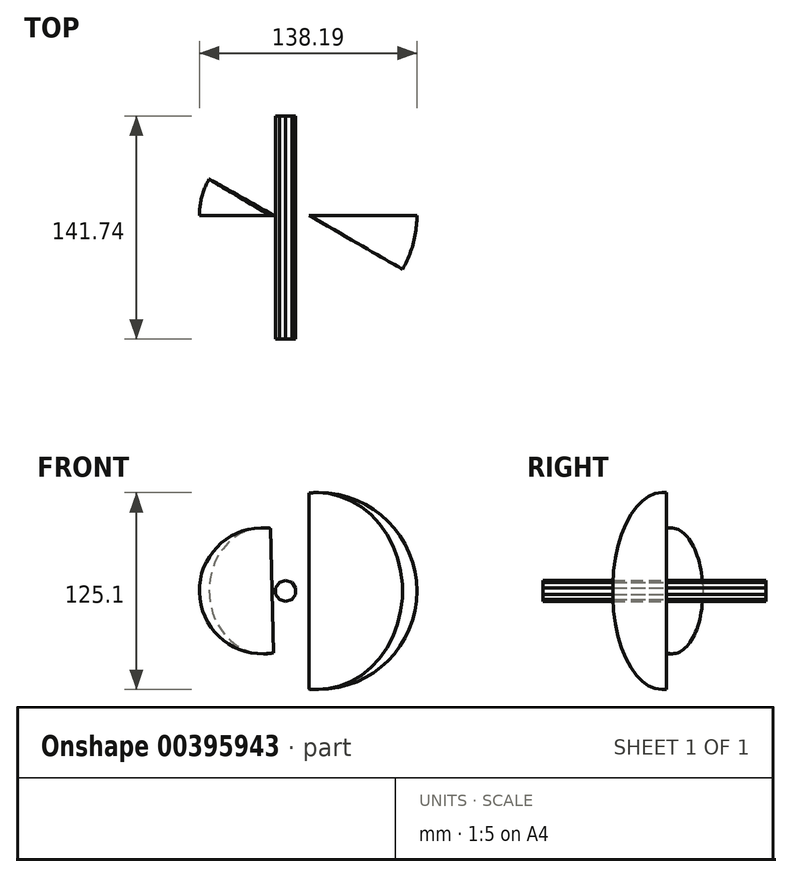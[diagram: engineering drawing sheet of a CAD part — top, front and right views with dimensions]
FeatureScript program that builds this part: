
annotation { "Feature Type Name" : "Feature", "Feature Type Description" : "" }
export const myFeature = defineFeature(function(context is Context, id is Id, definition is map)
    precondition{}
    {
        {
            var Q0;
            Q0=qCreatedBy(makeId("Front.planeOp"),FACE);
            var sketch = newSketch(context, id + "F0", { "sketchPlane" : qUnion([Q0])});
            skLineSegment(sketch, "E0", {"start": v(0, 75.87) * mm, "end": v(0, -48.68) * mm});
            skArc(sketch, "E1", {"start": v(0, -48.68) * mm, "mid": v(68.4, 13.6) * mm, "end": v(0, 75.87) * mm});
            skSolve(sketch);
        }
        {
            var Q0;
            Q0=makeQuery(id+"F0.imprint","IMPRINT",FACE,{"disambiguationData":[TD([[makeQuery(id+"F0.imprint","IMPRINT",EDGE,{"derivedFrom":sQuery(id+"F0.wireOp",EDGE,"E0")}),1.0]])]});
            var Q1;
            Q1=sQuery(id+"F0.wireOp",EDGE,"E0");
            revolve(context, id + "F1", {"entities" : qUnion([Q0]), "axis" : qUnion([Q1]), "revolveType" : RevolveType.ONE_DIRECTION, "angle" : 30 * degree});
        }
        {
            var Q0;
            Q0=qCreatedBy(makeId("Front.planeOp"),FACE);
            var sketch = newSketch(context, id + "F2", { "sketchPlane" : qUnion([Q0])});
            skLineSegment(sketch, "E2", {"start": v(-24.44, 53.4) * mm, "end": v(-22.66, -25.62) * mm});
            skArc(sketch, "E3", {"start": v(-24.44, 53.4) * mm, "mid": v(-69.77, 12.86) * mm, "end": v(-22.66, -25.62) * mm});
            skSolve(sketch);
        }
        {
            var Q0;
            Q0=makeQuery(id+"F2.imprint","IMPRINT",FACE,{"disambiguationData":[TD([[makeQuery(id+"F2.imprint","IMPRINT",EDGE,{"derivedFrom":sQuery(id+"F2.wireOp",EDGE,"E2")}),-1.0]])]});
            var Q1;
            Q1=sQuery(id+"F2.wireOp",EDGE,"E2");
            revolve(context, id + "F3", {"entities" : qUnion([Q0]), "axis" : qUnion([Q1]), "revolveType" : RevolveType.ONE_DIRECTION, "angle" : 30 * degree});
        }
        {
            var Q0;
            Q0=qCreatedBy(makeId("Front.planeOp"),FACE);
            var sketch = newSketch(context, id + "F4", { "sketchPlane" : qUnion([Q0])});
            skCircle(sketch, "E4.cCircle", {"center": v(-14.98, 13.6) * mm, "radius": 6.3 * mm, "construction": true});
            skLineSegment(sketch, "E4.0", {"start": v(-8.67, 15.65) * mm, "end": v(-8.67, 11.55) * mm});
            skLineSegment(sketch, "E4.1", {"start": v(-8.67, 11.55) * mm, "end": v(-11.08, 8.23) * mm});
            skLineSegment(sketch, "E4.2", {"start": v(-11.08, 8.23) * mm, "end": v(-14.98, 6.97) * mm});
            skLineSegment(sketch, "E4.3", {"start": v(-14.98, 6.97) * mm, "end": v(-18.87, 8.23) * mm});
            skLineSegment(sketch, "E4.4", {"start": v(-18.87, 8.23) * mm, "end": v(-21.28, 11.55) * mm});
            skLineSegment(sketch, "E4.5", {"start": v(-21.28, 11.55) * mm, "end": v(-21.28, 15.65) * mm});
            skLineSegment(sketch, "E4.6", {"start": v(-21.28, 15.65) * mm, "end": v(-18.87, 18.96) * mm});
            skLineSegment(sketch, "E4.7", {"start": v(-18.87, 18.96) * mm, "end": v(-14.98, 20.23) * mm});
            skLineSegment(sketch, "E4.8", {"start": v(-14.98, 20.23) * mm, "end": v(-11.08, 18.96) * mm});
            skLineSegment(sketch, "E4.9", {"start": v(-11.08, 18.96) * mm, "end": v(-8.67, 15.65) * mm});
            skPoint(sketch, "E4.0.midPoint", {"position": v(-8.67, 13.6) * mm});
            skSolve(sketch);
        }
        {
            var Q0;
            Q0=makeQuery(id+"F4.imprint","IMPRINT",FACE,{"disambiguationData":[TD([[makeQuery(id+"F4.imprint","IMPRINT",EDGE,{"derivedFrom":sQuery(id+"F4.wireOp",EDGE,"E4.0")}),-1.0]])]});
            extrude(context, id + "F5", {"entities" : qUnion([Q0]), "depth" : 53.1 * mm});
        }
        {
            var Q0;
            Q0=makeQuery(id+"F5.opExtrude","CAP_FACE",FACE,{"disambiguationData":[OSD([sQuery(id+"F4.wireOp",EDGE,"E4.0"),sQuery(id+"F4.wireOp",EDGE,"E4.1"),sQuery(id+"F4.wireOp",EDGE,"E4.2"),sQuery(id+"F4.wireOp",EDGE,"E4.3"),sQuery(id+"F4.wireOp",EDGE,"E4.4"),sQuery(id+"F4.wireOp",EDGE,"E4.5"),sQuery(id+"F4.wireOp",EDGE,"E4.6"),sQuery(id+"F4.wireOp",EDGE,"E4.7"),sQuery(id+"F4.wireOp",EDGE,"E4.8"),sQuery(id+"F4.wireOp",EDGE,"E4.9")])],"isStart":false});
            extrude(context, id + "F6", {"entities" : qUnion([Q0]), "operationType" : NewBodyOperationType.ADD, "depth" : 25.4 * mm});
        }
        {
            var Q0;
            Q0=makeQuery(id+"F5.opExtrude","CAP_FACE",FACE,{"disambiguationData":[OSD([sQuery(id+"F4.wireOp",EDGE,"E4.0"),sQuery(id+"F4.wireOp",EDGE,"E4.1"),sQuery(id+"F4.wireOp",EDGE,"E4.2"),sQuery(id+"F4.wireOp",EDGE,"E4.3"),sQuery(id+"F4.wireOp",EDGE,"E4.4"),sQuery(id+"F4.wireOp",EDGE,"E4.5"),sQuery(id+"F4.wireOp",EDGE,"E4.6"),sQuery(id+"F4.wireOp",EDGE,"E4.7"),sQuery(id+"F4.wireOp",EDGE,"E4.8"),sQuery(id+"F4.wireOp",EDGE,"E4.9")])],"isStart":true});
            extrude(context, id + "F7", {"entities" : qUnion([Q0]), "operationType" : NewBodyOperationType.ADD, "depth" : 63.25 * mm});
        }
    });
